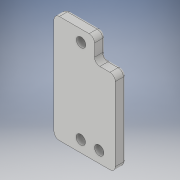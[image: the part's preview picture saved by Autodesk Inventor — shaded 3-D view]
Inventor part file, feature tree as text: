
AUTODESK INVENTOR PART (.ipt)
format: ipt  version: 2018 (Build 220112000, 112)  size: 157,696 bytes
history: native  units: in
note: dims shown in document units (in); Inventor stores cm internally (conversion verified against a paired STEP export)
features: other x3, sketch x2, fillet x1, plane x1
ambient origin geometry x8: Origin, YZ Plane, XZ Plane, XY Plane, X Axis, Y Axis, Z Axis, Center Point
bodies: Solid1 (feature_tree)
feature tree (7):
  other  "SyringeServoBaseClamp.ipt"
  fillet  "Fillet1"  Radius=0.3937in
  other  "Solid2::SyringeServoBaseClamp.ipt"
  other  "TaggingFeature1"
  sketch  "Sketch5"  dims[d1=0.0787in]
  sketch  "Sketch6"
  plane  "Work Plane1"
